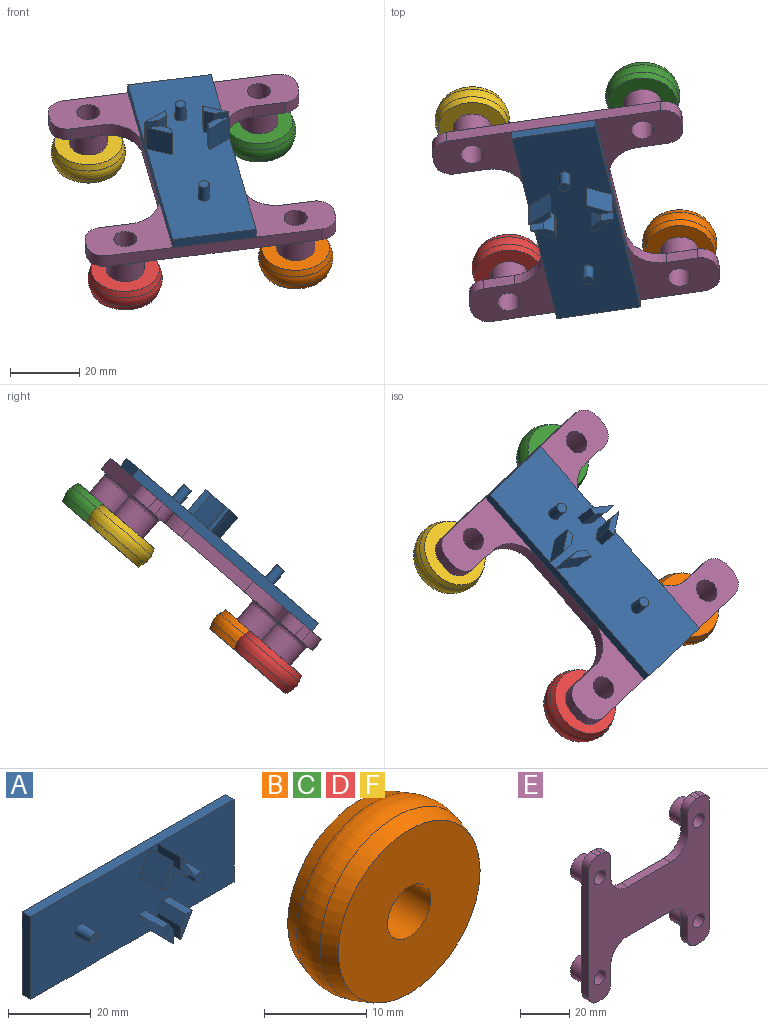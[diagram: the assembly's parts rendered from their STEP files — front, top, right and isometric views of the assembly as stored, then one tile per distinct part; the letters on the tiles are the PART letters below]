
ASSEMBLY  parts=6 mates=5
PART A: 34 faces, bbox 69.6x11x24.5 mm
  f0: cylinder r=10mm len=3mm, axis (0,-1,0), area 0.6mm2, adj f1,f7,f8,f9
  f1: plane 22.41x3mm, normal (0,0,-1), area 67.2mm2, adj f0,f2,f8,f9
  f2: plane 24.46x3mm, normal (1,0,0), area 73.4mm2, adj f1,f3,f8,f9
  f3: plane 69.6x3mm, normal (0,0,1), area 208.8mm2, adj f2,f4,f8,f9
  f4: plane 24.46x3mm, normal (-1,0,0), area 73.4mm2, adj f3,f5,f8,f9
  f5: plane 22.41x3mm, normal (0,0,-1), area 67.2mm2, adj f4,f6,f8,f9
  f6: cylinder r=10mm len=3mm, axis (0,-1,0), area 0.6mm2, adj f5,f7,f8,f9
  f7: plane 24.4x11mm, normal (0,0,-1), area 73.2mm2, adj f0,f6,f8,f9,f22,f23,f24,f25
  f8: plane 69.6x24.46mm, normal (0,-1,0), area 1640.3mm2, adj f0,f1,f2,f3,f4,f5,f6,f7
  f9: plane 69.6x24.46mm, normal (0,1,0), area 1702.1mm2, adj f0,f1,f2,f3,f4,f5,f6,f7
  f10: plane 8x2.78mm, normal (-0.87,0,-0.5), area 25.7mm2, adj f8,f11,f13,f14
  f11: plane 8x2.31mm, normal (0,0,-1), area 18.5mm2, adj f8,f10,f12,f14
  f12: plane 8x6.78mm, normal (0.87,0,0.5), area 62.6mm2, adj f8,f11,f13,f14
  f13: plane 8x4mm, normal (-1,0,0), area 32mm2, adj f8,f10,f12,f14
  f14: plane 6.78x3.92mm, normal (0,-1,0), area 11mm2, adj f10,f11,f12,f13
  f15: plane 8x6.78mm, normal (-0.87,0,0.5), area 62.6mm2, adj f8,f16,f18,f19
  f16: plane 8x2.31mm, normal (0,0,-1), area 18.5mm2, adj f8,f15,f17,f19
  f17: plane 8x2.78mm, normal (0.87,0,-0.5), area 25.7mm2, adj f8,f16,f18,f19
  f18: plane 8x4mm, normal (1,0,0), area 32mm2, adj f8,f15,f17,f19
  f19: plane 6.78x3.92mm, normal (0,-1,0), area 11mm2, adj f15,f16,f17,f18
  f20: plane 8x2.78mm, normal (0.87,0,0.5), area 25.7mm2, adj f8,f21,f23,f24
  f21: plane 8x2.31mm, normal (0,0,1), area 18.5mm2, adj f8,f20,f22,f24
  f22: plane 8x6.78mm, normal (-0.87,0,-0.5), area 62.6mm2, adj f7,f8,f21,f24
  f23: plane 8x4mm, normal (1,0,0), area 32mm2, adj f7,f8,f20,f24
  f24: plane 6.78x3.92mm, normal (0,-1,0), area 11mm2, adj f7,f20,f21,f22,f23
  f25: plane 8x6.78mm, normal (0.87,0,-0.5), area 62.6mm2, adj f7,f8,f26,f29
  f26: plane 8x2.31mm, normal (0,0,1), area 18.5mm2, adj f8,f25,f27,f29
  f27: plane 8x2.78mm, normal (-0.87,0,0.5), area 25.7mm2, adj f8,f26,f28,f29
  f28: plane 8x4mm, normal (-1,0,0), area 32mm2, adj f7,f8,f27,f29
  f29: plane 6.78x3.92mm, normal (0,-1,0), area 11mm2, adj f7,f25,f26,f27,f28
  f30: cone r=1.5mm half-angle=2deg, axis (0,1,0), area 49.9mm2, adj f8,f31
  f31: plane 3x3mm, normal (0,-1,0), area 7.1mm2, adj f30
  f32: cone r=1.5mm half-angle=2deg, axis (0,1,0), area 49.9mm2, adj f8,f33
  f33: plane 3x3mm, normal (0,-1,0), area 7.1mm2, adj f32
PART B: 6 faces, bbox 23.2x7x23.2 mm
  f0: cylinder r=3mm len=7mm, axis (0,-1,0), area 131.9mm2, adj f1,f4
  f1: plane 19.62x19.62mm, normal (0,1,0), area 274mm2, adj f0,f2
  f2: cone r=9.81mm half-angle=18.8deg, axis (0,-1,0), area 126.8mm2, adj f1,f5
  f3: cone r=11mm half-angle=18.8deg, axis (0,1,0), area 126.8mm2, adj f4,f5
  f4: plane 19.62x19.62mm, normal (0,-1,0), area 274mm2, adj f0,f3
  f5: torus R=5.72mm, axis (0,1,0), area 219.2mm2, adj f2,f3
PART C: same geometry as B
PART D: same geometry as B
PART E: 58 faces, bbox 72.1x11.5x72.9 mm
  f0: plane 12.6x9.85mm, normal (0,1,0), area 67.6mm2, adj f9,f10,f11,f38,f39,f44
  f1: plane 69.6x46.8mm, normal (0,1,0), area 2169.8mm2, adj f5,f6,f7,f9,f11,f12,f13,f15
  f2: plane 12.6x9.85mm, normal (0,1,0), area 67.6mm2, adj f7,f8,f9,f36,f37,f47
  f3: plane 12.6x9.85mm, normal (0,1,0), area 67.6mm2, adj f13,f14,f15,f40,f41,f56
  f4: plane 4x2.6mm, normal (0,0,-1), area 10.4mm2, adj f20,f21,f34,f35
  f5: plane 9.22x4.02mm, normal (1,0,0), area 36.8mm2, adj f1,f20,f21,f30,f35,f53
  f6: plane 24.4x4mm, normal (0,0,-1), area 97.6mm2, adj f1,f20,f30,f31
  f7: plane 9.22x4.02mm, normal (-1,0,0), area 36.8mm2, adj f1,f2,f20,f31,f36,f46
  f8: plane 4x2.6mm, normal (0,0,-1), area 10.4mm2, adj f2,f20,f36,f37
  f9: plane 62.92x4.02mm, normal (1,0,0), area 251.6mm2, adj f0,f1,f2,f20,f37,f38,f45,f49
  f10: plane 4x2.6mm, normal (0,0,1), area 10.4mm2, adj f0,f20,f38,f39
  f11: plane 9.22x4.02mm, normal (-1,0,0), area 36.8mm2, adj f0,f1,f20,f32,f39,f42
  f12: plane 24.4x4mm, normal (0,0,1), area 97.6mm2, adj f1,f20,f32,f33
  f13: plane 9.22x4.02mm, normal (1,0,0), area 36.8mm2, adj f1,f3,f20,f33,f40,f57
  f14: plane 4x2.6mm, normal (0,0,1), area 10.4mm2, adj f3,f20,f40,f41
  f15: plane 62.92x4.02mm, normal (-1,0,0), area 251.6mm2, adj f1,f3,f20,f21,f34,f41,f50,f54
  f16: cylinder r=3.3mm len=11.5mm, axis (0,-1,0), area 238.4mm2, adj f20,f23
  f17: cylinder r=3.3mm len=11.5mm, axis (0,-1,0), area 238.4mm2, adj f20,f29
  f18: cylinder r=3.3mm len=11.5mm, axis (0,-1,0), area 238.4mm2, adj f20,f27
  f19: cylinder r=3.3mm len=11.5mm, axis (0,-1,0), area 238.4mm2, adj f20,f25
  f20: plane 72.9x69.6mm, normal (0,-1,0), area 2831mm2, adj f4,f5,f6,f7,f8,f9,f10,f11
  f21: plane 12.6x9.85mm, normal (0,1,0), area 67.6mm2, adj f4,f5,f15,f34,f35,f51
  f22: cylinder r=5.5mm len=11mm, axis (0,-1,0), area 224.6mm2, adj f23,f54,f55,f56,f57
  f23: plane 11x11mm, normal (0,1,0), area 60.8mm2, adj f16,f22
  f24: cylinder r=5.5mm len=11mm, axis (0,-1,0), area 224.6mm2, adj f25,f50,f51,f52,f53
  f25: plane 11x11mm, normal (0,1,0), area 60.8mm2, adj f19,f24
  f26: cylinder r=5.5mm len=11mm, axis (0,-1,0), area 224.6mm2, adj f27,f46,f47,f48,f49
  f27: plane 11x11mm, normal (0,1,0), area 60.8mm2, adj f18,f26
  f28: cylinder r=5.5mm len=11mm, axis (0,-1,0), area 224.6mm2, adj f29,f42,f43,f44,f45
  f29: plane 11x11mm, normal (0,1,0), area 60.8mm2, adj f17,f28
  f30: cylinder r=10mm len=10mm, axis (0,1,0), area 62.8mm2, adj f1,f5,f6,f20
  f31: cylinder r=10mm len=10mm, axis (0,-1,0), area 62.8mm2, adj f1,f6,f7,f20
  f32: cylinder r=10mm len=10mm, axis (0,1,0), area 62.8mm2, adj f1,f11,f12,f20
  f33: cylinder r=10mm len=10mm, axis (0,-1,0), area 62.8mm2, adj f1,f12,f13,f20
  f34: cylinder r=5mm len=5mm, axis (0,-1,0), area 31.4mm2, adj f4,f15,f20,f21
  f35: cylinder r=5mm len=5mm, axis (0,-1,0), area 31.4mm2, adj f4,f5,f20,f21
  f36: cylinder r=5mm len=5mm, axis (0,-1,0), area 31.4mm2, adj f2,f7,f8,f20
  f37: cylinder r=5mm len=5mm, axis (0,1,0), area 31.4mm2, adj f2,f8,f9,f20
  f38: cylinder r=5mm len=5mm, axis (0,-1,0), area 31.4mm2, adj f0,f9,f10,f20
  f39: cylinder r=5mm len=5mm, axis (0,-1,0), area 31.4mm2, adj f0,f10,f11,f20
  f40: cylinder r=5mm len=5mm, axis (0,-1,0), area 31.4mm2, adj f3,f13,f14,f20
  f41: cylinder r=5mm len=5mm, axis (0,1,0), area 31.4mm2, adj f3,f14,f15,f20
  f42: bspline ~3.86x1.1mm, area 4.1mm2, adj f11,f28,f43,f44
  f43: torus R=6.5mm, axis (0,-1,0), area 24.4mm2, adj f1,f28,f42,f45
  f44: torus R=6.5mm, axis (0,-1,0), area 24.4mm2, adj f0,f28,f42,f45
  f45: bspline ~3.86x1.1mm, area 4.1mm2, adj f9,f28,f43,f44
  f46: bspline ~3.86x1.1mm, area 4.1mm2, adj f7,f26,f47,f48
  f47: torus R=6.5mm, axis (0,-1,0), area 24.4mm2, adj f2,f26,f46,f49
  f48: torus R=6.5mm, axis (0,-1,0), area 24.4mm2, adj f1,f26,f46,f49
  f49: bspline ~3.86x1.1mm, area 4.1mm2, adj f9,f26,f47,f48
  f50: bspline ~3.86x1.1mm, area 4.1mm2, adj f15,f24,f51,f52
  f51: torus R=6.5mm, axis (0,-1,0), area 24.4mm2, adj f21,f24,f50,f53
  f52: torus R=6.5mm, axis (0,-1,0), area 24.4mm2, adj f1,f24,f50,f53
  f53: bspline ~3.86x1.1mm, area 4.1mm2, adj f5,f24,f51,f52
  f54: bspline ~3.86x1.1mm, area 4.1mm2, adj f15,f22,f55,f56
  f55: torus R=6.5mm, axis (0,-1,0), area 24.4mm2, adj f1,f22,f54,f57
  f56: torus R=6.5mm, axis (0,-1,0), area 24.4mm2, adj f3,f22,f54,f57
  f57: bspline ~3.86x1.1mm, area 4.1mm2, adj f13,f22,f55,f56
PART F: same geometry as B
PLACE A rot(axis=(-0.33,-0.86,0.39),109.1deg) t=(471.05,285.32,158.73)mm
PLACE B rot(axis=(-0.33,-0.86,0.39),109.1deg) t=(530.82,249.94,128.28)mm
PLACE C rot(axis=(-0.33,-0.86,0.39),109.1deg) t=(520.2,292.38,164.81)mm
PLACE D rot(axis=(-0.33,-0.86,0.39),109.1deg) t=(481.7,242.87,122.2)mm
PLACE E rot(axis=(-0.33,-0.86,0.39),109.1deg) t=(471.07,285.32,158.73)mm
PLACE F rot(axis=(-0.33,-0.86,0.39),109.1deg) t=(471.07,285.32,158.73)mm
MATE fastened F.f0 <-> E.f17  axis (0,-0.65,0.76) through (143.31,449.13,-0.86)mm
MATE fastened A.f9 <-> E.f20  axis (0,0.65,-0.76) through (173.19,423.94,-7.37)mm
MATE fastened D.f0 <-> E.f16  axis (0,-0.65,0.76) through (153.94,406.69,-37.39)mm
MATE fastened C.f0 <-> E.f18  axis (0,-0.65,0.76) through (192.44,456.2,5.22)mm
MATE fastened B.f0 <-> E.f19  axis (0,-0.65,0.76) through (203.06,413.75,-31.31)mm
